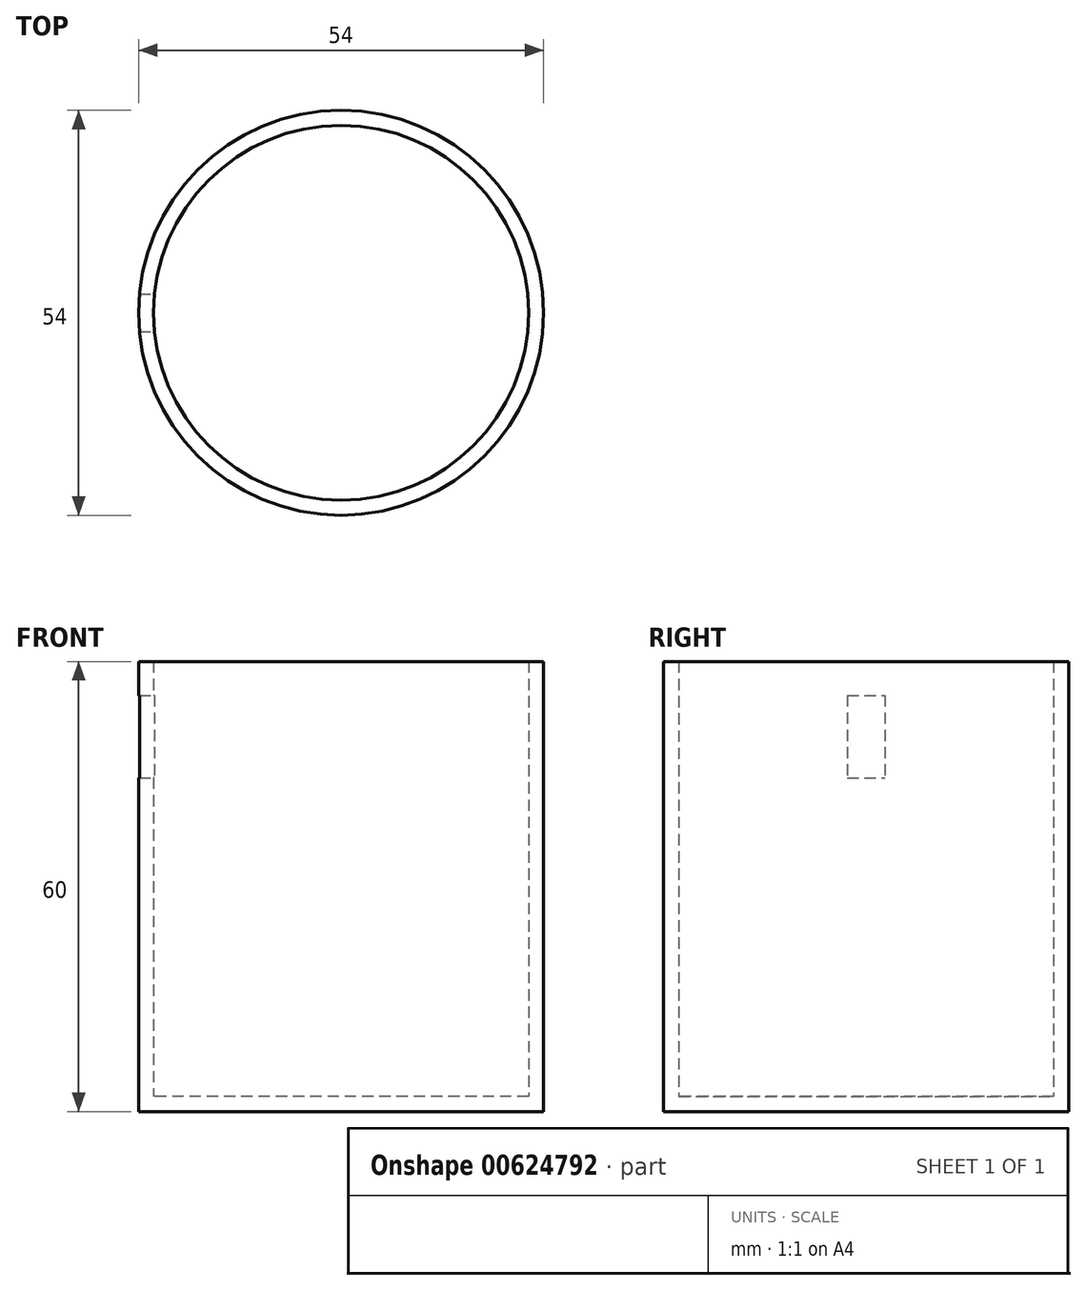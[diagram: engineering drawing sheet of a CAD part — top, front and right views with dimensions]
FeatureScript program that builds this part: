
annotation { "Feature Type Name" : "Feature", "Feature Type Description" : "" }
export const myFeature = defineFeature(function(context is Context, id is Id, definition is map)
    precondition{}
    {
        {
            var Q0;
            Q0=qCreatedBy(makeId("Top.planeOp"),FACE);
            var sketch = newSketch(context, id + "F0", { "sketchPlane" : qUnion([Q0])});
            skCircle(sketch, "E0", {"center": v(0, 0) * mm, "radius": 25 * mm});
            skCircle(sketch, "E1.0", {"center": v(0, 0) * mm, "radius": 27 * mm});
            skSolve(sketch);
        }
        {
            var Q0;
            Q0=makeQuery(id+"F0.imprint","IMPRINT",FACE,{"disambiguationData":[TD([[makeQuery(id+"F0.imprint","IMPRINT",EDGE,{"derivedFrom":sQuery(id+"F0.wireOp",EDGE,"E0")}),-1.0]])]});
            extrude(context, id + "F1", {"entities" : qUnion([Q0]), "depth" : 60 * mm, "offsetDistance" : 25 * mm});
        }
        {
            var Q0;
            Q0=qCreatedBy(makeId("Right.planeOp"),FACE);
            var sketch = newSketch(context, id + "F2", { "sketchPlane" : qUnion([Q0])});
            skLineSegment(sketch, "E2.bottom", {"start": v(-2.5, 55.5) * mm, "end": v(2.5, 55.5) * mm});
            skLineSegment(sketch, "E2.top", {"start": v(-2.5, 44.5) * mm, "end": v(2.5, 44.5) * mm});
            skLineSegment(sketch, "E2.left", {"start": v(-2.5, 55.5) * mm, "end": v(-2.5, 44.5) * mm});
            skLineSegment(sketch, "E2.right", {"start": v(2.5, 55.5) * mm, "end": v(2.5, 44.5) * mm});
            skLineSegment(sketch, "E3", {"start": v(-17, 50) * mm, "end": v(16.98, 50) * mm, "construction": true});
            skSolve(sketch);
        }
        {
            var Q0;
            Q0=qSketchRegion(id+"F2",true);
            extrude(context, id + "F3", {"entities" : qUnion([Q0]), "operationType" : NewBodyOperationType.REMOVE, "oppositeDirection" : true, "depth" : 25 * mm, "offsetDistance" : 25 * mm});
        }
        {
            var Q0;
            Q0 = qSketchRegion(id + "F2", true);
            extrude(context, id + "F4", {"entities" : qUnion([Q0]), "operationType" : NewBodyOperationType.REMOVE, "oppositeDirection" : true, "depth" : 30 * mm, "offsetDistance" : 25 * mm});
        }
        {
            var Q0;
            Q0=makeQuery(id+"F0.imprint","IMPRINT",FACE,{"disambiguationData":[TD([[makeQuery(id+"F0.imprint","IMPRINT",EDGE,{"derivedFrom":sQuery(id+"F0.wireOp",EDGE,"E0")}),1.0]])]});
            extrude(context, id + "F5", {"entities" : qUnion([Q0]), "operationType" : NewBodyOperationType.ADD, "depth" : 2 * mm, "offsetDistance" : 25 * mm});
        }
    });
